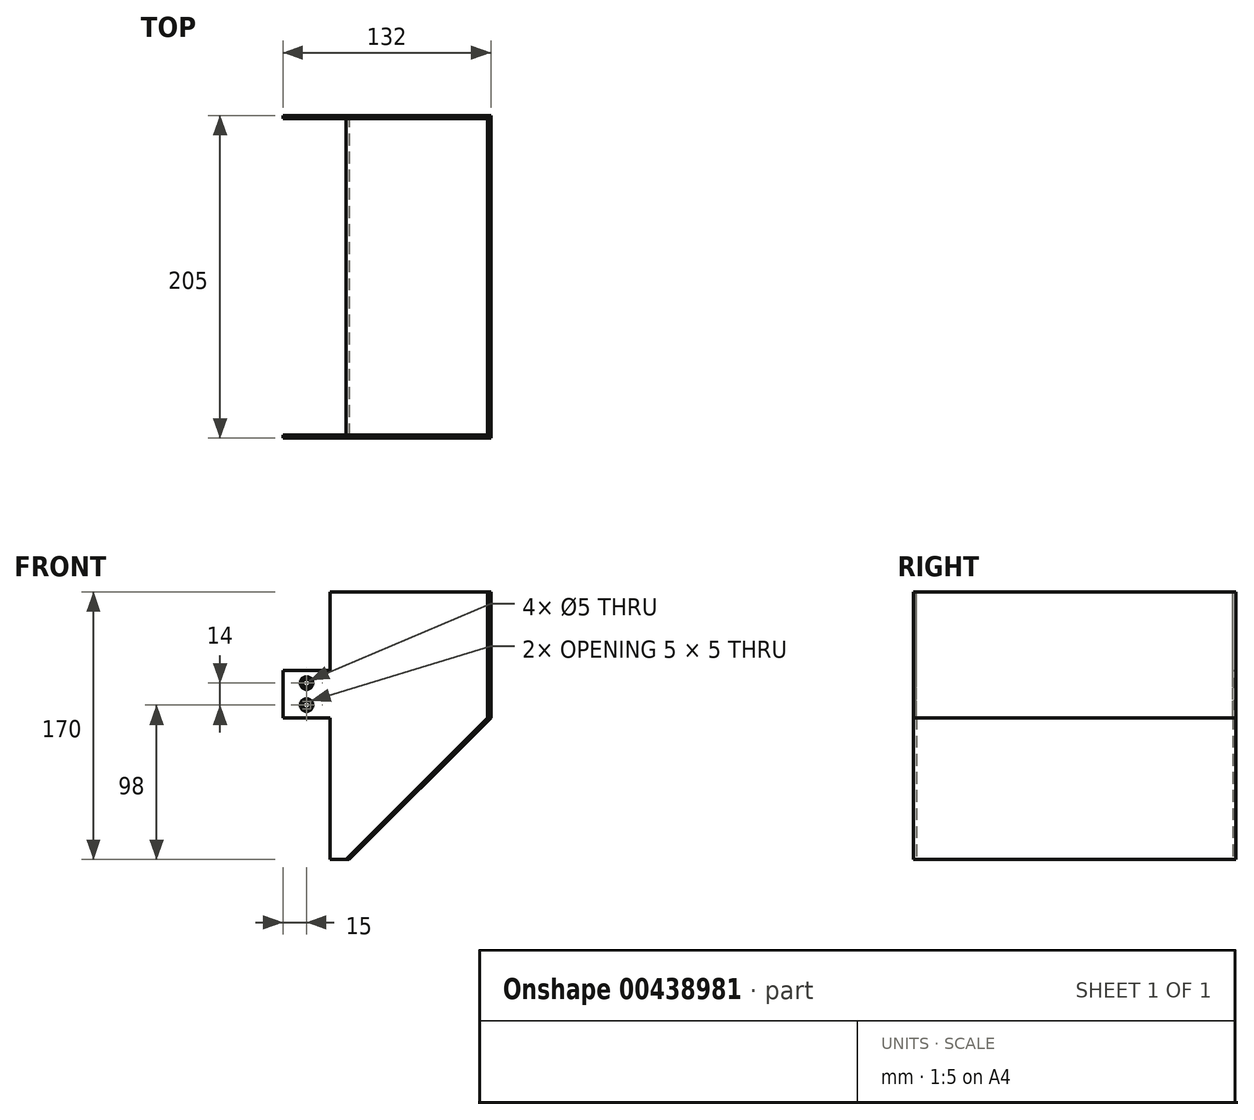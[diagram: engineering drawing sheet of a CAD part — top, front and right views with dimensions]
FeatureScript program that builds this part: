
annotation { "Feature Type Name" : "Feature", "Feature Type Description" : "" }
export const myFeature = defineFeature(function(context is Context, id is Id, definition is map)
    precondition{}
    {
        {
            var Q0;
            Q0=qCreatedBy(makeId("Front.planeOp"),FACE);
            var sketch = newSketch(context, id + "F0", { "sketchPlane" : qUnion([Q0])});
            skLineSegment(sketch, "E0", {"start": v(0, 0) * mm, "end": v(0, 30) * mm});
            skLineSegment(sketch, "E1", {"start": v(0, 30) * mm, "end": v(30, 30) * mm});
            skLineSegment(sketch, "E2", {"start": v(0, 0) * mm, "end": v(30, 0) * mm});
            skLineSegment(sketch, "E3", {"start": v(30, 30) * mm, "end": v(30, 0) * mm, "construction": true});
            skPoint(sketch, "E4", {"position": v(15, 22) * mm});
            skPoint(sketch, "E5", {"position": v(15, 8) * mm});
            skLineSegment(sketch, "E6", {"start": v(30, 30) * mm, "end": v(30, 80) * mm});
            skLineSegment(sketch, "E7", {"start": v(30, 80) * mm, "end": v(130, 80) * mm});
            skLineSegment(sketch, "E8", {"start": v(30, 0) * mm, "end": v(30, -90) * mm});
            skLineSegment(sketch, "E9", {"start": v(30, -90) * mm, "end": v(40, -90) * mm});
            skLineSegment(sketch, "E10", {"start": v(130, 0) * mm, "end": v(130, 80) * mm});
            skLineSegment(sketch, "E11", {"start": v(130, 0) * mm, "end": v(40, -90) * mm});
            skSolve(sketch);
        }
        {
            var Q0;
            Q0=makeQuery(id+"F0.imprint","IMPRINT",FACE,{"disambiguationData":[TD([[makeQuery(id+"F0.imprint","IMPRINT",EDGE,{"derivedFrom":sQuery(id+"F0.wireOp",EDGE,"E0")}),-1.0]])]});
            extrude(context, id + "F1", {"entities" : qUnion([Q0]), "depth" : 2 * mm});
        }
        {
            var Q0;
            Q0=makeQuery(id+"F1.opExtrude","CAP_FACE",FACE,{"disambiguationData":[OSD([sQuery(id+"F0.wireOp",EDGE,"E0"),sQuery(id+"F0.wireOp",EDGE,"E1"),sQuery(id+"F0.wireOp",EDGE,"E2"),sQuery(id+"F0.wireOp",EDGE,"RuK3nLGE-273N-dLGN-qRqw-R5OvAwTtNyxc")])],"isStart":true});
            var sketch = newSketch(context, id + "F2", { "sketchPlane" : qUnion([Q0])});
            skPoint(sketch, "E12", {"position": v(-15, 22) * mm});
            skPoint(sketch, "E13", {"position": v(-15, 8) * mm});
            skSolve(sketch);
        }
        {
            var Q0;
            Q0=sQuery(id+"F2.wireOp",VERTEX,"E12");
            var Q1;
            Q1=sQuery(id+"F2.wireOp",VERTEX,"E13");
            var Q2;
            Q2=makeQuery(id+"F1.opExtrude","SWEPT_BODY",BODY,{"disambiguationData":[OSD([sQuery(id+"F0.wireOp",EDGE,"E0"),sQuery(id+"F0.wireOp",EDGE,"E1"),sQuery(id+"F0.wireOp",EDGE,"E2"),sQuery(id+"F0.wireOp",EDGE,"RuK3nLGE-273N-dLGN-qRqw-R5OvAwTtNyxc")])]});
            hole(context, id + "F3", {"style" : HoleStyle.C_SINK, "endStyle" : HoleEndStyle.BLIND, "holeDiameter" : 5 * mm, "cSinkDiameter" : 8 * mm, "cSinkAngle" : 90 * degree, "holeDepth" : 10 * mm, "isTappedThrough" : true, "tappedDepth" : 12 * mm, "tapClearance" : 3, "startFromSketch" : true, "locations" : qUnion([Q0, Q1]), "scope" : qUnion([Q2])});
        }
        {
            var Q0;
            Q0=qCreatedBy(makeId("Front.planeOp"),FACE);
            cPlane(context, id + "F4", {"entities" : qUnion([Q0]), "cplaneType" : CPlaneType.OFFSET, "offset" : 102.5 * mm, "width" : 150 * mm, "height" : 150 * mm});
        }
        {
            var Q0;
            Q0=makeQuery(id+"F1.opExtrude","SWEPT_BODY",BODY,{"disambiguationData":[OSD([sQuery(id+"F0.wireOp",EDGE,"E0"),sQuery(id+"F0.wireOp",EDGE,"E1"),sQuery(id+"F0.wireOp",EDGE,"E2"),sQuery(id+"F0.wireOp",EDGE,"RuK3nLGE-273N-dLGN-qRqw-R5OvAwTtNyxc")])]});
            var Q1;
            Q1=qCreatedBy(id+"F4.planeOp",FACE);
            mirror(context, id + "F5", {"entities" : qUnion([Q0]), "mirrorPlane" : qUnion([Q1])});
        }
        {
            var Q0;
            Q0=qCreatedBy(makeId("Right.planeOp"),FACE);
            cPlane(context, id + "F6", {"entities" : qUnion([Q0]), "cplaneType" : CPlaneType.OFFSET, "offset" : 130 * mm, "width" : 150 * mm, "height" : 150 * mm});
        }
        {
            var Q0;
            Q0=qCreatedBy(id+"F6.planeOp",FACE);
            var sketch = newSketch(context, id + "F7", { "sketchPlane" : qUnion([Q0])});
            skLineSegment(sketch, "E14", {"start": v(-205, 80) * mm, "end": v(0, 80) * mm});
            skLineSegment(sketch, "E15", {"start": v(0, 80) * mm, "end": v(0, 0) * mm});
            skLineSegment(sketch, "E16", {"start": v(0, 0) * mm, "end": v(-205, 0) * mm});
            skLineSegment(sketch, "E17", {"start": v(-205, 0) * mm, "end": v(-205, 80) * mm});
            skSolve(sketch);
        }
        {
            var Q0;
            Q0=makeQuery(id+"F7.imprint","IMPRINT",FACE,{"disambiguationData":[TD([[makeQuery(id+"F7.imprint","IMPRINT",EDGE,{"derivedFrom":sQuery(id+"F7.wireOp",EDGE,"E14")}),-1.0]])]});
            extrude(context, id + "F8", {"entities" : qUnion([Q0]), "depth" : 2 * mm});
        }
        {
            var Q0;
            Q0=makeQuery(id+"F8.opExtrude","SWEPT_FACE",FACE,{"disambiguationData":[OSD([sQuery(id+"F7.wireOp",EDGE,"E17")])]});
            var sketch = newSketch(context, id + "F9", { "sketchPlane" : qUnion([Q0])});
            skLineSegment(sketch, "E18", {"start": v(130, 0) * mm, "end": v(40, -90) * mm});
            skLineSegment(sketch, "E19", {"start": v(130, 0) * mm, "end": v(132, 0) * mm});
            skLineSegment(sketch, "E20", {"start": v(132, 0) * mm, "end": v(42, -90) * mm});
            skLineSegment(sketch, "E21", {"start": v(40, -90) * mm, "end": v(42, -90) * mm});
            skSolve(sketch);
        }
        {
            var Q0;
            Q0=makeQuery(id+"F9.imprint","IMPRINT",FACE,{"disambiguationData":[TD([[makeQuery(id+"F9.imprint","IMPRINT",EDGE,{"derivedFrom":sQuery(id+"F9.wireOp",EDGE,"E18")}),1.0]])]});
            extrude(context, id + "F10", {"entities" : qUnion([Q0]), "oppositeDirection" : true, "depth" : 205 * mm});
        }
    });
